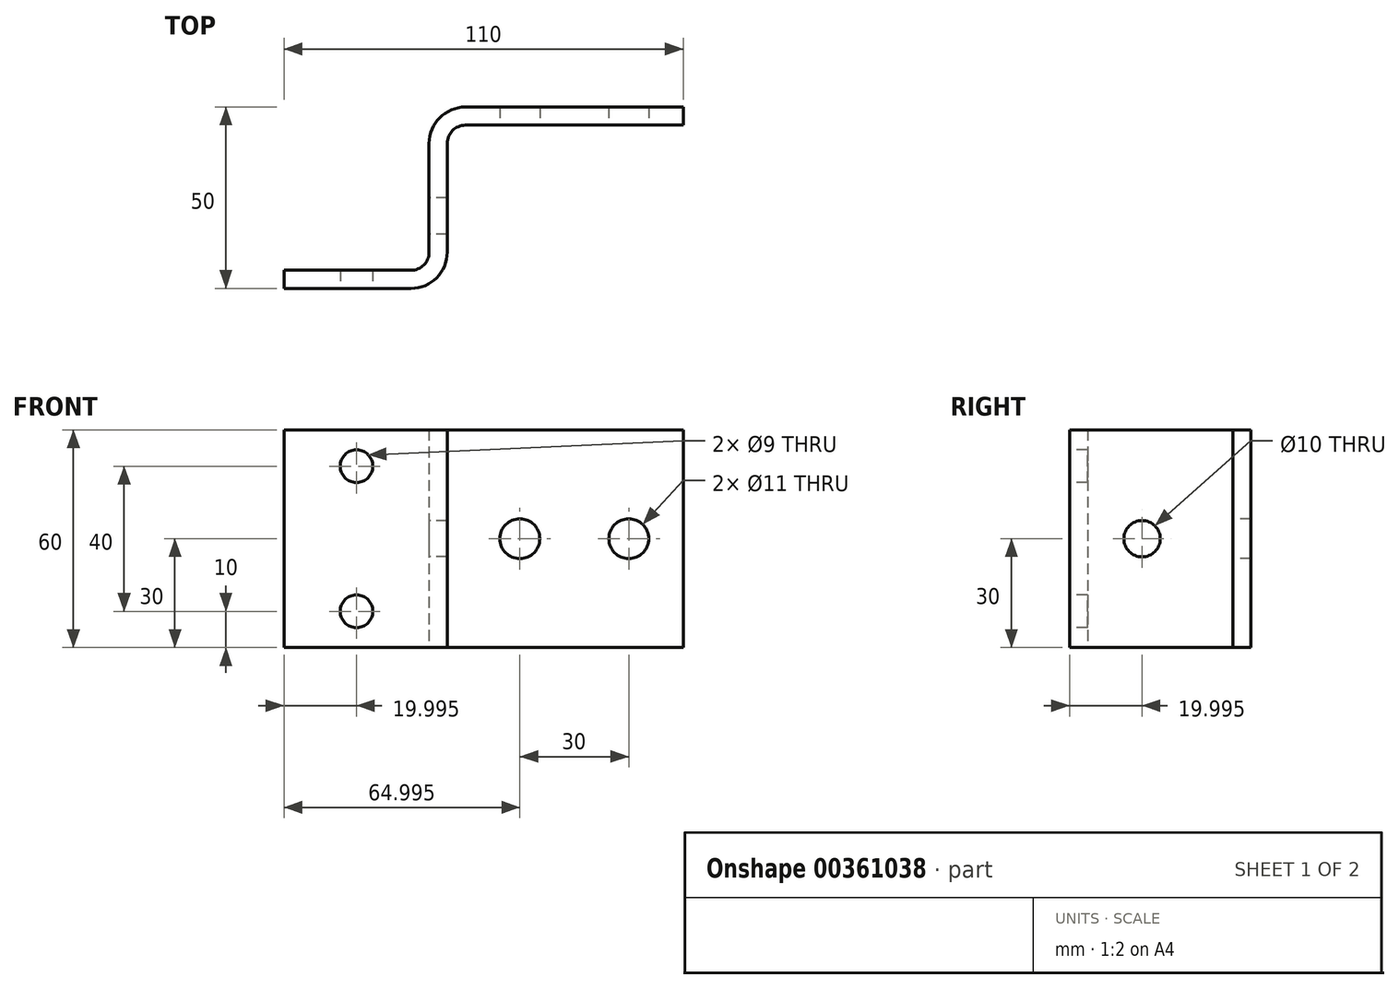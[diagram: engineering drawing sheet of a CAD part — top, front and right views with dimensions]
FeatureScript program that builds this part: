
annotation { "Feature Type Name" : "Feature", "Feature Type Description" : "" }
export const myFeature = defineFeature(function(context is Context, id is Id, definition is map)
    precondition{}
    {
        {
            var Q0;
            Q0=qCreatedBy(makeId("Top.planeOp"),FACE);
            var sketch = newSketch(context, id + "F0", { "sketchPlane" : qUnion([Q0])});
            skLineSegment(sketch, "E0", {"start": v(29.86, 23.32) * mm, "end": v(29.86, 28.32) * mm});
            skLineSegment(sketch, "E1", {"start": v(29.86, 28.32) * mm, "end": v(-30.14, 28.32) * mm});
            skLineSegment(sketch, "E2", {"start": v(-40.14, 18.32) * mm, "end": v(-40.14, -11.68) * mm});
            skLineSegment(sketch, "E3", {"start": v(29.86, 23.32) * mm, "end": v(-30.14, 23.32) * mm});
            skLineSegment(sketch, "E4", {"start": v(-45.14, -16.68) * mm, "end": v(-80.14, -16.68) * mm});
            skLineSegment(sketch, "E5", {"start": v(-80.14, -16.68) * mm, "end": v(-80.14, -21.68) * mm});
            skLineSegment(sketch, "E6", {"start": v(-80.14, -21.68) * mm, "end": v(-45.14, -21.68) * mm});
            skLineSegment(sketch, "E7", {"start": v(-35.14, -11.68) * mm, "end": v(-35.14, 18.32) * mm});
            skPoint(sketch, "E8.visualSharp", {"position": v(-40.14, 28.32) * mm});
            skArc(sketch, "E8.filletArc", {"start": v(-30.14, 28.32) * mm, "mid": v(-37.22, 25.39) * mm, "end": v(-40.14, 18.32) * mm});
            skPoint(sketch, "E9.visualSharp", {"position": v(-35.14, -21.68) * mm});
            skArc(sketch, "E9.filletArc", {"start": v(-45.14, -21.68) * mm, "mid": v(-38.07, -18.76) * mm, "end": v(-35.14, -11.68) * mm});
            skPoint(sketch, "E10.visualSharp", {"position": v(-40.14, -16.68) * mm});
            skArc(sketch, "E10.filletArc", {"start": v(-45.14, -16.68) * mm, "mid": v(-41.6, -15.22) * mm, "end": v(-40.14, -11.68) * mm});
            skPoint(sketch, "E11.visualSharp", {"position": v(-35.14, 23.32) * mm});
            skArc(sketch, "E11.filletArc", {"start": v(-30.14, 23.32) * mm, "mid": v(-33.68, 21.85) * mm, "end": v(-35.14, 18.32) * mm});
            skSolve(sketch);
        }
        {
            var Q0;
            Q0 = qSketchRegion(id + "F0", true);
            extrude(context, id + "F1", {"entities" : qUnion([Q0]), "depth" : 60 * mm});
        }
        {
            var Q0;
            Q0=makeQuery(id+"F1.opExtrude","SWEPT_FACE",FACE,{"disambiguationData":[OSD([sQuery(id+"F0.wireOp",EDGE,"E6")])]});
            var sketch = newSketch(context, id + "F2", { "sketchPlane" : qUnion([Q0])});
            skPoint(sketch, "E12", {"position": v(-60.14, 50) * mm});
            skCircle(sketch, "E13", {"center": v(-60.14, 50) * mm, "radius": 4.5 * mm});
            skPoint(sketch, "E14", {"position": v(-60.14, 10) * mm});
            skPoint(sketch, "E15.end.orphan", {"position": v(-60.14, 60) * mm});
            skPoint(sketch, "E16.end.orphan", {"position": v(-80.14, 50) * mm});
            skCircle(sketch, "E17", {"center": v(-60.14, 10) * mm, "radius": 4.5 * mm});
            skSolve(sketch);
        }
        {
            var Q0;
            Q0 = qSketchRegion(id + "F2", true);
            extrude(context, id + "F3", {"entities" : qUnion([Q0]), "operationType" : NewBodyOperationType.REMOVE, "oppositeDirection" : true, "depth" : 25 * mm});
        }
        {
            var Q0;
            Q0=makeQuery(id+"F1.opExtrude","SWEPT_FACE",FACE,{"disambiguationData":[OSD([sQuery(id+"F0.wireOp",EDGE,"E3")])]});
            var sketch = newSketch(context, id + "F4", { "sketchPlane" : qUnion([Q0])});
            skLineSegment(sketch, "E18", {"start": v(29.86, 60) * mm, "end": v(14.86, 60) * mm});
            skLineSegment(sketch, "E19", {"start": v(29.86, 60) * mm, "end": v(29.86, 30) * mm});
            skPoint(sketch, "E20", {"position": v(14.86, 30) * mm});
            skCircle(sketch, "E21", {"center": v(14.86, 30) * mm, "radius": 5.5 * mm});
            skPoint(sketch, "E22", {"position": v(-15.14, 30) * mm});
            skCircle(sketch, "E23", {"center": v(-15.14, 30) * mm, "radius": 5.5 * mm});
            skSolve(sketch);
        }
        {
            var Q0;
            Q0 = qSketchRegion(id + "F4", true);
            extrude(context, id + "F5", {"entities" : qUnion([Q0]), "operationType" : NewBodyOperationType.REMOVE, "oppositeDirection" : true, "depth" : 25 * mm});
        }
        {
            var Q0;
            Q0=makeQuery(id+"F1.opExtrude","SWEPT_FACE",FACE,{"disambiguationData":[OSD([sQuery(id+"F0.wireOp",EDGE,"E2")])]});
            var sketch = newSketch(context, id + "F6", { "sketchPlane" : qUnion([Q0])});
            skLineSegment(sketch, "E24", {"start": v(11.68, 60) * mm, "end": v(1.68, 60) * mm});
            skLineSegment(sketch, "E25", {"start": v(11.68, 60) * mm, "end": v(11.68, 30) * mm});
            skCircle(sketch, "E26", {"center": v(1.68, 30) * mm, "radius": 5 * mm});
            skPoint(sketch, "E27.end.orphan", {"position": v(21.68, 60) * mm});
            skSolve(sketch);
        }
        {
            var Q0;
            Q0 = qSketchRegion(id + "F6", true);
            extrude(context, id + "F7", {"entities" : qUnion([Q0]), "operationType" : NewBodyOperationType.REMOVE, "oppositeDirection" : true, "depth" : 25 * mm});
        }
    });
